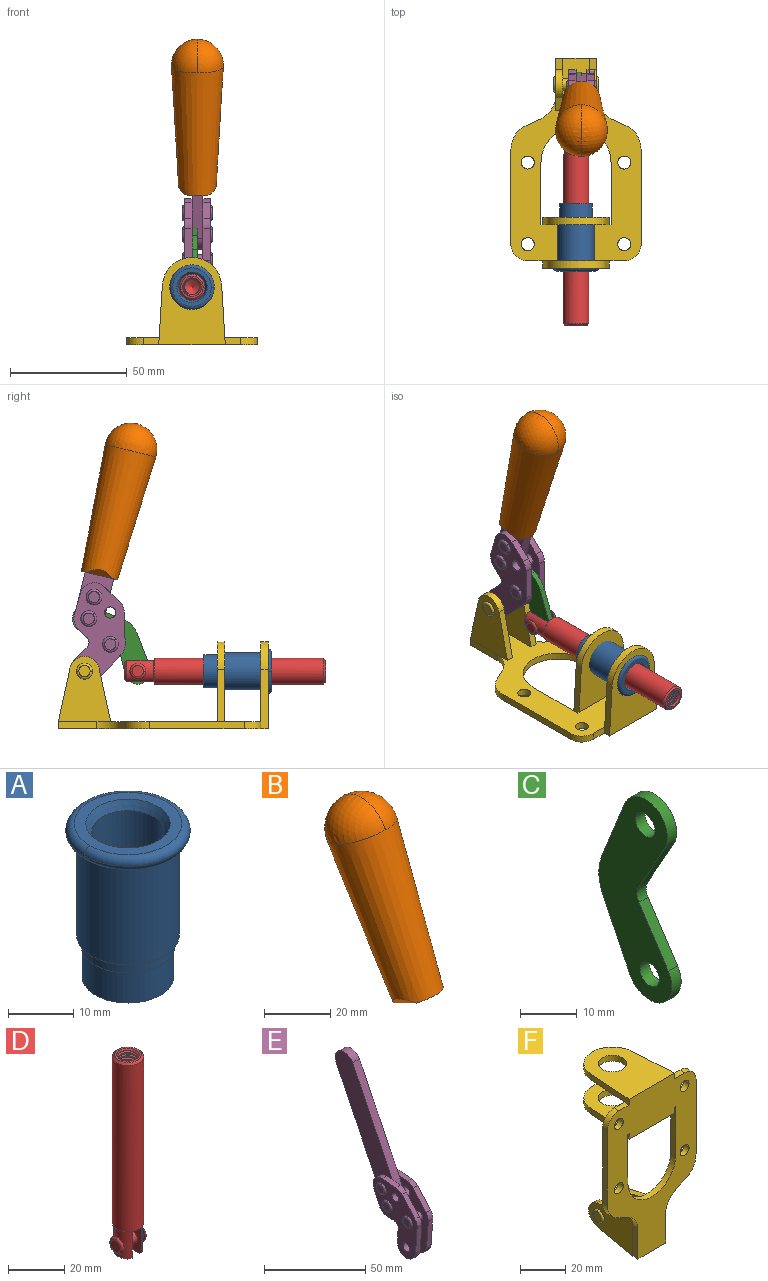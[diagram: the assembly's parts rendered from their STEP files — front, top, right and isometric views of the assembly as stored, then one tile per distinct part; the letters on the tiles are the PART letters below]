
ASSEMBLY  parts=6 mates=5
PART A: 15 faces, bbox 20.6x20.6x28.7 mm
  f0: torus R=8.26mm, axis (0,0,1), area 56.8mm2, adj f1,f10,f12
  f1: torus R=8.26mm, axis (0,0,1), area 56.8mm2, adj f0,f6,f13
  f2: cylinder r=5.59mm len=25.91mm, axis (0,0,1), area 909.6mm2, adj f3,f4
  f3: cone r=6.86mm half-angle=45deg, axis (0,0,-1), area 70.2mm2, adj f2,f14
  f4: cone r=6.47mm half-angle=30deg, axis (0,0,1), area 66.7mm2, adj f2,f13
  f5: cylinder r=7.04mm len=14.07mm, axis (0,0,1), area 252.6mm2, adj f11,f14
  f6: torus R=8.26mm, axis (0,0,1), area 56.8mm2, adj f1,f12,f13
  f7: cylinder r=7.16mm len=14.33mm, axis (0,0,1), area 91.5mm2, adj f9,f11
  f8: cylinder r=7.86mm len=18.42mm, axis (0,0,1), area 909.6mm2, adj f9,f10
  f9: plane 15.72x15.72mm, normal (0,0,-1), area 33mm2, adj f7,f8
  f10: plane 16.51x16.51mm, normal (0,0,-1), area 19.9mm2, adj f0,f8,f12
  f11: plane 14.33x14.33mm, normal (0,0,-1), area 5.7mm2, adj f5,f7
  f12: torus R=8.26mm, axis (0,0,1), area 56.8mm2, adj f0,f6,f10
  f13: plane 16.51x16.51mm, normal (0,0,1), area 82.7mm2, adj f1,f4,f6
  f14: plane 14.07x14.07mm, normal (0,0,-1), area 7.8mm2, adj f3,f5
PART B: 11 faces, bbox 22.3x42.6x64.5 mm
  f0: sphere r=11.13mm, area 411.4mm2, adj f1,f8
  f1: cone r=11.11mm half-angle=3.3deg, axis (0,0.44,0.9), area 3251.8mm2, adj f0,f7,f8,f9,f10
  f2: cylinder r=6.16mm len=11.7mm, axis (1,0,0), area 89.5mm2, adj f3,f4,f5,f6
  f3: plane 60.23x36.75mm, normal (-1,0,0), area 763.6mm2, adj f2,f4,f6,f10
  f4: plane 51.37x25.05mm, normal (0,0.9,-0.44), area 264.2mm2, adj f2,f3,f5,f10
  f5: plane 60.23x36.75mm, normal (1,0,0), area 763.6mm2, adj f2,f4,f6,f10
  f6: plane 51.37x25.05mm, normal (0,-0.9,0.44), area 264.2mm2, adj f2,f3,f5,f10
  f7: plane 9.95x5.95mm, normal (0.71,-0.31,-0.64), area 25.8mm2, adj f1,f10
  f8: sphere r=11.13mm, area 411.4mm2, adj f0,f1
  f9: plane 9.95x5.95mm, normal (-0.71,-0.31,-0.64), area 25.8mm2, adj f1,f10
  f10: plane 14.27x11.38mm, normal (0,-0.44,-0.9), area 106.7mm2, adj f1,f3,f4,f5,f6,f7,f9
PART C: 12 faces, bbox 2.3x18.2x42.8 mm
  f0: cylinder r=2.4mm len=4.8mm, axis (1,0,0), area 34.9mm2, adj f4,f11
  f1: cylinder r=10.41mm len=8.47mm, axis (1,0,0), area 20.2mm2, adj f4,f9,f10,f11
  f2: cylinder r=3.05mm len=3.16mm, axis (1,0,0), area 7.7mm2, adj f4,f6,f7,f11
  f3: cylinder r=2.4mm len=4.8mm, axis (1,0,0), area 34.9mm2, adj f4,f11
  f4: plane 42.81x18.23mm, normal (-1,0,0), area 414.1mm2, adj f0,f1,f2,f3,f5,f6,f7,f8
  f5: cylinder r=5.54mm len=10.67mm, axis (1,0,0), area 41.8mm2, adj f4,f6,f10,f11
  f6: plane 11.66x6.53mm, normal (0,-0.87,-0.49), area 30.9mm2, adj f2,f4,f5,f11
  f7: plane 11.17x7.33mm, normal (0,-0.84,0.55), area 30.9mm2, adj f2,f4,f8,f11
  f8: cylinder r=5.54mm len=10.51mm, axis (1,0,0), area 41.8mm2, adj f4,f7,f9,f11
  f9: plane 13.67x6.67mm, normal (0,0.9,-0.44), area 35.1mm2, adj f1,f4,f8,f11
  f10: plane 14.1x5.7mm, normal (0,0.93,0.37), area 35.1mm2, adj f1,f4,f5,f11
  f11: plane 42.81x18.23mm, normal (1,0,0), area 414.1mm2, adj f0,f1,f2,f3,f5,f6,f7,f8
PART D: 48 faces, bbox 12.6x11.1x86.1 mm
  f0: torus R=2.41mm, axis (-1,0,0), area 15mm2, adj f30,f32,f34
  f1: torus R=2.41mm, axis (-1,0,0), area 15mm2, adj f29,f31,f33
  f2: cylinder r=5.54mm len=72.39mm, axis (0,0,1), area 2518.5mm2, adj f3,f4,f42,f43
  f3: cone r=5.54mm half-angle=45deg, axis (0,0,1), area 7.6mm2, adj f2,f5,f41
  f4: cone r=5.54mm half-angle=45deg, axis (0,0,-1), area 34.9mm2, adj f2,f39
  f5: cylinder r=5.08mm len=11.48mm, axis (0,0,1), area 108.3mm2, adj f3,f7,f8,f41
  f6: cylinder r=2.41mm len=4.83mm, axis (-1,0,0), area 71.2mm2, adj f40,f41
  f7: cylinder r=2.41mm len=4.83mm, axis (-1,0,0), area 7.6mm2, adj f5,f34
  f8: cone r=5.08mm half-angle=45deg, axis (0,0,1), area 10.6mm2, adj f5,f37,f41
  f9: cone r=3.98mm half-angle=45deg, axis (0,0,1), area 17.6mm2, adj f27,f39,f45,f46,f47
  f10: cylinder r=2.41mm len=4.83mm, axis (-1,0,0), area 7.6mm2, adj f33,f38
  f11: cylinder r=3.2mm len=6.4mm, axis (0,0,1), area 78.4mm2, adj f12,f28,f44,f45,f47
  f12: cylinder r=3.2mm len=6.4mm, axis (0,0,1), area 10.5mm2, adj f11,f13,f45,f47
  f13: cylinder r=3.2mm len=6.4mm, axis (0,0,1), area 10.5mm2, adj f12,f14,f45,f47
  f14: cylinder r=3.2mm len=6.4mm, axis (0,0,1), area 10.5mm2, adj f13,f15,f45,f47
  f15: cylinder r=3.2mm len=6.4mm, axis (0,0,1), area 10.5mm2, adj f14,f16,f45,f47
  f16: cylinder r=3.2mm len=6.4mm, axis (0,0,1), area 10.5mm2, adj f15,f17,f45,f47
  f17: cylinder r=3.2mm len=6.4mm, axis (0,0,1), area 10.5mm2, adj f16,f18,f45,f47
  f18: cylinder r=3.2mm len=6.4mm, axis (0,0,1), area 10.5mm2, adj f17,f19,f45,f47
  f19: cylinder r=3.2mm len=6.4mm, axis (0,0,1), area 10.5mm2, adj f18,f20,f45,f47
  f20: cylinder r=3.2mm len=6.4mm, axis (0,0,1), area 10.5mm2, adj f19,f21,f45,f47
  f21: cylinder r=3.2mm len=6.4mm, axis (0,0,1), area 10.5mm2, adj f20,f22,f45,f47
  f22: cylinder r=3.2mm len=6.4mm, axis (0,0,1), area 10.5mm2, adj f21,f23,f45,f47
  f23: cylinder r=3.2mm len=6.4mm, axis (0,0,1), area 10.5mm2, adj f22,f24,f45,f47
  f24: cylinder r=3.2mm len=6.4mm, axis (0,0,1), area 10.5mm2, adj f23,f25,f45,f47
  f25: cylinder r=3.2mm len=6.4mm, axis (0,0,1), area 10.5mm2, adj f24,f26,f45,f47
  f26: cylinder r=3.2mm len=6.4mm, axis (0,0,1), area 10.5mm2, adj f25,f27,f45,f47
  f27: cylinder r=3.2mm len=6.4mm, axis (0,0,1), area 7.4mm2, adj f9,f26,f45,f47
  f28: cone r=3.2mm half-angle=60deg, axis (0,0,1), area 37.2mm2, adj f11
  f29: plane 4.83x4.83mm, normal (-1,0,0), area 18.3mm2, adj f1,f31
  f30: plane 4.83x4.83mm, normal (1,0,0), area 18.3mm2, adj f0,f32
  f31: torus R=2.41mm, axis (-1,0,0), area 15mm2, adj f1,f29,f33
  f32: torus R=2.41mm, axis (-1,0,0), area 15mm2, adj f0,f30,f34
  f33: plane 6.83x6.83mm, normal (1,0,0), area 18.3mm2, adj f1,f10,f31
  f34: plane 6.83x6.83mm, normal (-1,0,0), area 18.3mm2, adj f0,f7,f32
  f35: cone r=5.08mm half-angle=45deg, axis (0,0,1), area 10.6mm2, adj f36,f38,f40
  f36: plane 7.25x1.97mm, normal (0,0,-1), area 10mm2, adj f35,f40
  f37: plane 7.25x1.97mm, normal (0,0,-1), area 10mm2, adj f8,f41
  f38: cylinder r=5.08mm len=11.48mm, axis (0,0,1), area 108.3mm2, adj f10,f35,f40,f42
  f39: plane 9.55x9.55mm, normal (0,0,1), area 22mm2, adj f4,f9
  f40: plane 12.76x10.09mm, normal (1,0,0), area 95.7mm2, adj f6,f35,f36,f38,f42,f43
  f41: plane 12.76x10.09mm, normal (-1,0,0), area 95.7mm2, adj f3,f5,f6,f8,f37,f43
  f42: cone r=5.54mm half-angle=45deg, axis (0,0,1), area 7.6mm2, adj f2,f38,f40
  f43: plane 11.07x4.7mm, normal (0,0,-1), area 50.4mm2, adj f2,f40,f41
  f44: plane 0.89x0.62mm, normal (-1,0,0), area 0.3mm2, adj f11,f45,f46,f47
  f45: bspline ~24.8x7.63mm, area 266.6mm2, adj f9,f11,f12,f13,f14,f15,f16,f17
  f46: bspline ~24.87x7.63mm, area 73.6mm2, adj f9,f44,f45,f47
  f47: bspline ~24.98x7.63mm, area 272.5mm2, adj f9,f11,f12,f13,f14,f15,f16,f17
PART E: 59 faces, bbox 12.9x60.2x99.6 mm
  f0: torus R=2.39mm, axis (-1,0,0), area 14.9mm2, adj f20,f43,f51
  f1: torus R=2.39mm, axis (-1,0,0), area 14.9mm2, adj f19,f42,f51
  f2: torus R=2.39mm, axis (-1,0,0), area 14.9mm2, adj f18,f35,f51
  f3: torus R=2.39mm, axis (-1,0,0), area 14.9mm2, adj f14,f17,f23
  f4: torus R=2.39mm, axis (-1,0,0), area 14.9mm2, adj f13,f16,f23
  f5: torus R=2.39mm, axis (-1,0,0), area 14.9mm2, adj f12,f15,f23
  f6: cylinder r=2.39mm len=4.78mm, axis (1,0,0), area 46.5mm2, adj f48,f50,f51
  f7: cylinder r=2.39mm len=4.78mm, axis (1,0,0), area 46.5mm2, adj f50,f51
  f8: cylinder r=6.35mm len=12.68mm, axis (1,0,0), area 61.8mm2, adj f38,f39,f50,f51
  f9: cylinder r=2.39mm len=4.78mm, axis (-1,0,0), area 70.5mm2, adj f46,f50
  f10: cylinder r=2.39mm len=4.78mm, axis (-1,0,0), area 46.5mm2, adj f23,f45,f46
  f11: cylinder r=2.39mm len=4.78mm, axis (-1,0,0), area 46.5mm2, adj f23,f46
  f12: plane 4.78x4.78mm, normal (1,0,0), area 17.9mm2, adj f5,f15
  f13: plane 4.78x4.78mm, normal (1,0,0), area 17.9mm2, adj f4,f16
  f14: plane 4.78x4.78mm, normal (1,0,0), area 17.9mm2, adj f3,f17
  f15: torus R=2.39mm, axis (-1,0,0), area 14.9mm2, adj f5,f12,f23
  f16: torus R=2.39mm, axis (-1,0,0), area 14.9mm2, adj f4,f13,f23
  f17: torus R=2.39mm, axis (-1,0,0), area 14.9mm2, adj f3,f14,f23
  f18: plane 4.78x4.78mm, normal (-1,0,0), area 17.9mm2, adj f2,f35
  f19: plane 4.78x4.78mm, normal (-1,0,0), area 17.9mm2, adj f1,f42
  f20: plane 4.78x4.78mm, normal (-1,0,0), area 17.9mm2, adj f0,f43
  f21: plane 2.26x0.2mm, normal (1,0,0), area 0.2mm2, adj f31,f44
  f22: plane 2.26x0.2mm, normal (-1,0,0), area 0.2mm2, adj f41,f44
  f23: plane 39.37x30.77mm, normal (1,0,0), area 565.5mm2, adj f3,f4,f5,f10,f11,f15,f16,f17
  f24: cylinder r=6.1mm len=4.15mm, axis (-1,0,0), area 14.7mm2, adj f23,f25,f32,f46
  f25: plane 10.25x9.01mm, normal (0,-0.75,0.66), area 42.3mm2, adj f23,f24,f26,f46
  f26: cylinder r=6.35mm len=4.64mm, axis (-1,0,0), area 15.6mm2, adj f23,f25,f27,f46
  f27: plane 15.84x3.1mm, normal (0,-1,-0.07), area 49.2mm2, adj f23,f26,f28,f46
  f28: cylinder r=6.35mm len=12.68mm, axis (-1,0,0), area 61.8mm2, adj f23,f27,f29,f46
  f29: plane 8.11x3.1mm, normal (0,1,0.07), area 25.2mm2, adj f23,f28,f30,f46
  f30: cylinder r=3.05mm len=3.25mm, axis (-1,0,0), area 14.8mm2, adj f23,f29,f31,f46
  f31: plane 5.99x3.1mm, normal (0,0.07,-1), area 18.6mm2, adj f21,f23,f30,f44,f46
  f32: plane 9.5x3.1mm, normal (0,-0.07,1), area 29.5mm2, adj f23,f24,f33,f46,f47
  f33: cylinder r=6.1mm len=8.63mm, axis (-1,0,0), area 39.1mm2, adj f23,f32,f34,f47
  f34: plane 8.65x3.96mm, normal (0,0.91,-0.42), area 29.5mm2, adj f23,f33,f44,f47
  f35: torus R=2.39mm, axis (-1,0,0), area 14.9mm2, adj f2,f18,f51
  f36: plane 10.25x9.01mm, normal (0,-0.75,0.66), area 42.3mm2, adj f37,f49,f50,f51
  f37: cylinder r=6.35mm len=4.64mm, axis (1,0,0), area 15.6mm2, adj f36,f38,f50,f51
  f38: plane 15.84x3.1mm, normal (0,-1,-0.07), area 49.2mm2, adj f8,f37,f50,f51
  f39: plane 8.11x3.1mm, normal (0,1,0.07), area 25.2mm2, adj f8,f40,f50,f51
  f40: cylinder r=3.05mm len=3.25mm, axis (1,0,0), area 14.8mm2, adj f39,f41,f50,f51
  f41: plane 5.99x3.1mm, normal (0,0.07,-1), area 18.6mm2, adj f22,f40,f44,f50,f51
  f42: torus R=2.39mm, axis (-1,0,0), area 14.9mm2, adj f1,f19,f51
  f43: torus R=2.39mm, axis (-1,0,0), area 14.9mm2, adj f0,f20,f51
  f44: cylinder r=6.35mm len=12.12mm, axis (-1,0,0), area 128.9mm2, adj f21,f22,f23,f31,f34,f41,f46,f47
  f45: plane 2.65x1.35mm, normal (1,0,0), area 1mm2, adj f10,f55
  f46: plane 39.08x20.42mm, normal (-1,0,0), area 412.5mm2, adj f9,f10,f11,f24,f25,f26,f27,f28
  f47: plane 77.62x39.82mm, normal (1,0,0), area 850mm2, adj f32,f33,f34,f44,f53,f54,f55
  f48: plane 2.65x1.35mm, normal (-1,0,0), area 1mm2, adj f6,f55
  f49: cylinder r=6.1mm len=4.15mm, axis (1,0,0), area 14.7mm2, adj f36,f50,f51,f56
  f50: plane 39.08x20.42mm, normal (1,0,0), area 412.5mm2, adj f6,f7,f8,f9,f36,f37,f38,f39
  f51: plane 39.37x30.77mm, normal (-1,0,0), area 565.5mm2, adj f0,f1,f2,f6,f7,f8,f35,f36
  f52: plane 8.65x3.96mm, normal (0,0.91,-0.42), area 29.5mm2, adj f44,f51,f57,f58
  f53: plane 68.49x33.4mm, normal (0,0.9,-0.44), area 358.1mm2, adj f44,f47,f54,f58
  f54: cylinder r=6.35mm len=12.06mm, axis (1,0,0), area 93.7mm2, adj f47,f53,f55,f58
  f55: plane 68.49x33.4mm, normal (0,-0.9,0.44), area 358.1mm2, adj f44,f45,f46,f47,f48,f50,f54,f58
  f56: plane 9.5x3.1mm, normal (0,-0.07,1), area 29.5mm2, adj f49,f50,f51,f57,f58
  f57: cylinder r=6.1mm len=8.63mm, axis (1,0,0), area 39.1mm2, adj f51,f52,f56,f58
  f58: plane 77.62x39.82mm, normal (-1,0,0), area 850mm2, adj f44,f52,f53,f54,f55,f56,f57
PART F: 55 faces, bbox 55.7x37.4x89.8 mm
  f0: torus R=2.41mm, axis (-1,0,0), area 15mm2, adj f11,f15,f25
  f1: torus R=2.41mm, axis (-1,0,0), area 15mm2, adj f10,f12,f22
  f2: cylinder r=2.78mm len=5.56mm, axis (0,-1,0), area 54.2mm2, adj f30,f54
  f3: cylinder r=14.99mm len=29.97mm, axis (0,-1,0), area 145.9mm2, adj f30,f49,f53,f54
  f4: cylinder r=2.78mm len=5.56mm, axis (0,-1,0), area 54.2mm2, adj f30,f54
  f5: cylinder r=2.78mm len=5.56mm, axis (0,-1,0), area 54.2mm2, adj f30,f54
  f6: cylinder r=2.78mm len=5.56mm, axis (0,-1,0), area 54.2mm2, adj f30,f54
  f7: cylinder r=6.35mm len=12.7mm, axis (0,0,1), area 123.6mm2, adj f27,f51
  f8: cylinder r=6.35mm len=12.7mm, axis (0,0,-1), area 124.7mm2, adj f21,f35
  f9: cylinder r=2.41mm len=11.18mm, axis (-1,0,0), area 169.4mm2, adj f16,f19
  f10: plane 4.83x4.83mm, normal (1,0,0), area 18.3mm2, adj f1,f12
  f11: plane 4.83x4.83mm, normal (-1,0,0), area 18.3mm2, adj f0,f15
  f12: torus R=2.41mm, axis (-1,0,0), area 15mm2, adj f1,f10,f22
  f13: cylinder r=6.35mm len=12.41mm, axis (1,0,0), area 53.4mm2, adj f18,f19,f22,f23
  f14: cylinder r=6.35mm len=12.41mm, axis (-1,0,0), area 53.4mm2, adj f16,f17,f24,f25
  f15: torus R=2.41mm, axis (-1,0,0), area 15mm2, adj f0,f11,f25
  f16: plane 27.86x22.35mm, normal (1,0,0), area 425.4mm2, adj f9,f14,f17,f24,f30
  f17: plane 22.86x4.97mm, normal (0,0.21,0.98), area 72.5mm2, adj f14,f16,f25,f30
  f18: plane 22.86x4.97mm, normal (0,0.21,0.98), area 72.5mm2, adj f13,f19,f22,f30
  f19: plane 27.86x22.35mm, normal (-1,0,0), area 425.4mm2, adj f9,f13,f18,f23,f30
  f20: cylinder r=12.7mm len=25.35mm, axis (0,0,-1), area 119.8mm2, adj f21,f34,f35,f36
  f21: plane 34.21x28.07mm, normal (0,0,-1), area 702.4mm2, adj f8,f20,f30,f34,f36
  f22: plane 27.96x22.45mm, normal (1,0,0), area 407.2mm2, adj f1,f12,f13,f18,f23,f30,f42,f43
  f23: plane 22.86x4.97mm, normal (0,0.21,-0.98), area 72.5mm2, adj f13,f19,f22,f44
  f24: plane 22.86x4.97mm, normal (0,0.21,-0.98), area 72.5mm2, adj f14,f16,f25,f44
  f25: plane 27.86x22.35mm, normal (-1,0,0), area 407.1mm2, adj f0,f14,f15,f17,f24,f30,f45,f46
  f26: plane 3.1x0.95mm, normal (0,0,-1), area 2.7mm2, adj f30,f49,f50,f54
  f27: plane 34.21x28.07mm, normal (0,0,1), area 702.4mm2, adj f7,f28,f30,f50,f52
  f28: cylinder r=12.7mm len=25.35mm, axis (0,0,1), area 118.8mm2, adj f27,f50,f51,f52
  f29: plane 3.1x0.95mm, normal (0,0,-1), area 2.7mm2, adj f30,f52,f53,f54
  f30: plane 86.54x55.63mm, normal (0,1,0), area 2362.9mm2, adj f2,f3,f4,f5,f6,f16,f17,f18
  f31: plane 40.56x3.1mm, normal (-1,0,0), area 125.7mm2, adj f30,f32,f48,f54
  f32: cylinder r=7.11mm len=7.11mm, axis (0,-1,0), area 34.6mm2, adj f30,f31,f33,f54
  f33: plane 6.67x3.1mm, normal (0,0,1), area 20.4mm2, adj f30,f32,f34,f54
  f34: plane 25.39x3.13mm, normal (-1,0.06,0), area 79.5mm2, adj f20,f21,f33,f35,f54
  f35: plane 37.31x28.45mm, normal (0,0,1), area 789.9mm2, adj f8,f20,f34,f36,f54
  f36: plane 25.39x3.13mm, normal (1,0.06,0), area 79.5mm2, adj f20,f21,f35,f37,f54
  f37: plane 6.67x3.1mm, normal (0,0,1), area 20.4mm2, adj f30,f36,f38,f54
  f38: cylinder r=7.11mm len=7.11mm, axis (0,-1,0), area 34.6mm2, adj f30,f37,f39,f54
  f39: plane 40.56x3.1mm, normal (1,0,0), area 125.7mm2, adj f30,f38,f40,f54
  f40: cylinder r=11.18mm len=10.16mm, axis (0,-1,0), area 39.5mm2, adj f30,f39,f41,f54
  f41: plane 6.09x3.1mm, normal (0.42,0,-0.91), area 20.8mm2, adj f30,f40,f42,f54
  f42: cylinder r=11.18mm len=9.41mm, axis (0,-1,0), area 37.2mm2, adj f22,f30,f41,f43,f54
  f43: plane 16.5x3.1mm, normal (1,0,0), area 51.1mm2, adj f22,f42,f44,f54
  f44: plane 17.37x3.1mm, normal (0,0,-1), area 53.8mm2, adj f23,f24,f30,f43,f45,f54
  f45: plane 16.5x3.1mm, normal (-1,0,0), area 51.1mm2, adj f25,f44,f46,f54
  f46: cylinder r=11.18mm len=9.41mm, axis (0,-1,0), area 37.2mm2, adj f25,f30,f45,f47,f54
  f47: plane 6.09x3.1mm, normal (-0.42,0,-0.91), area 20.8mm2, adj f30,f46,f48,f54
  f48: cylinder r=11.18mm len=10.16mm, axis (0,-1,0), area 39.5mm2, adj f30,f31,f47,f54
  f49: plane 26.54x3.1mm, normal (-1,0,0), area 82.3mm2, adj f3,f26,f30,f54
  f50: plane 25.39x3.1mm, normal (1,0.06,0), area 78.8mm2, adj f26,f27,f28,f51,f54
  f51: plane 37.31x28.45mm, normal (0,0,-1), area 789.9mm2, adj f7,f28,f50,f52,f54
  f52: plane 25.39x3.1mm, normal (-1,0.06,0), area 78.8mm2, adj f27,f28,f29,f51,f54
  f53: plane 26.54x3.1mm, normal (1,0,0), area 82.3mm2, adj f3,f29,f30,f54
  f54: plane 89.66x55.63mm, normal (0,-1,0), area 2678.5mm2, adj f2,f3,f4,f5,f6,f26,f29,f31
PLACE A rot(axis=(1,0,0),90deg) t=(0,2.5,1.23)mm
PLACE B rot(axis=(1,0,0),40deg) t=(2.31,-6.15,34.64)mm
PLACE C rot(axis=(0,-0.4,-0.92),180deg) t=(1.16,38.45,19.74)mm
PLACE D rot(axis=(1,0,0),90deg) t=(0,26.01,1.23)mm
PLACE E rot(axis=(1,0,0),40deg) t=(2.35,-6.15,34.64)mm
PLACE F rot(axis=(1,0,0),90deg) t=(0,1.23,1.23)mm fixed
MATE slider D.f2 <-> F.f7  axis (0,-1,0) through (0,-32.78,25.84)mm
MATE fastened B.f2 <-> E.f54  axis (1,0,0) through (0,13.14,122.25)mm
MATE revolute C.f3 <-> D.f6  axis (1,0,0) through (0,10.53,25.84)mm
MATE revolute F.f0 <-> E.f7  axis (-1,0,0) through (0,33.32,25.84)mm
MATE fastened F.f7 <-> A.f2  axis (0,-1,0) through (0,-45.16,25.84)mm
